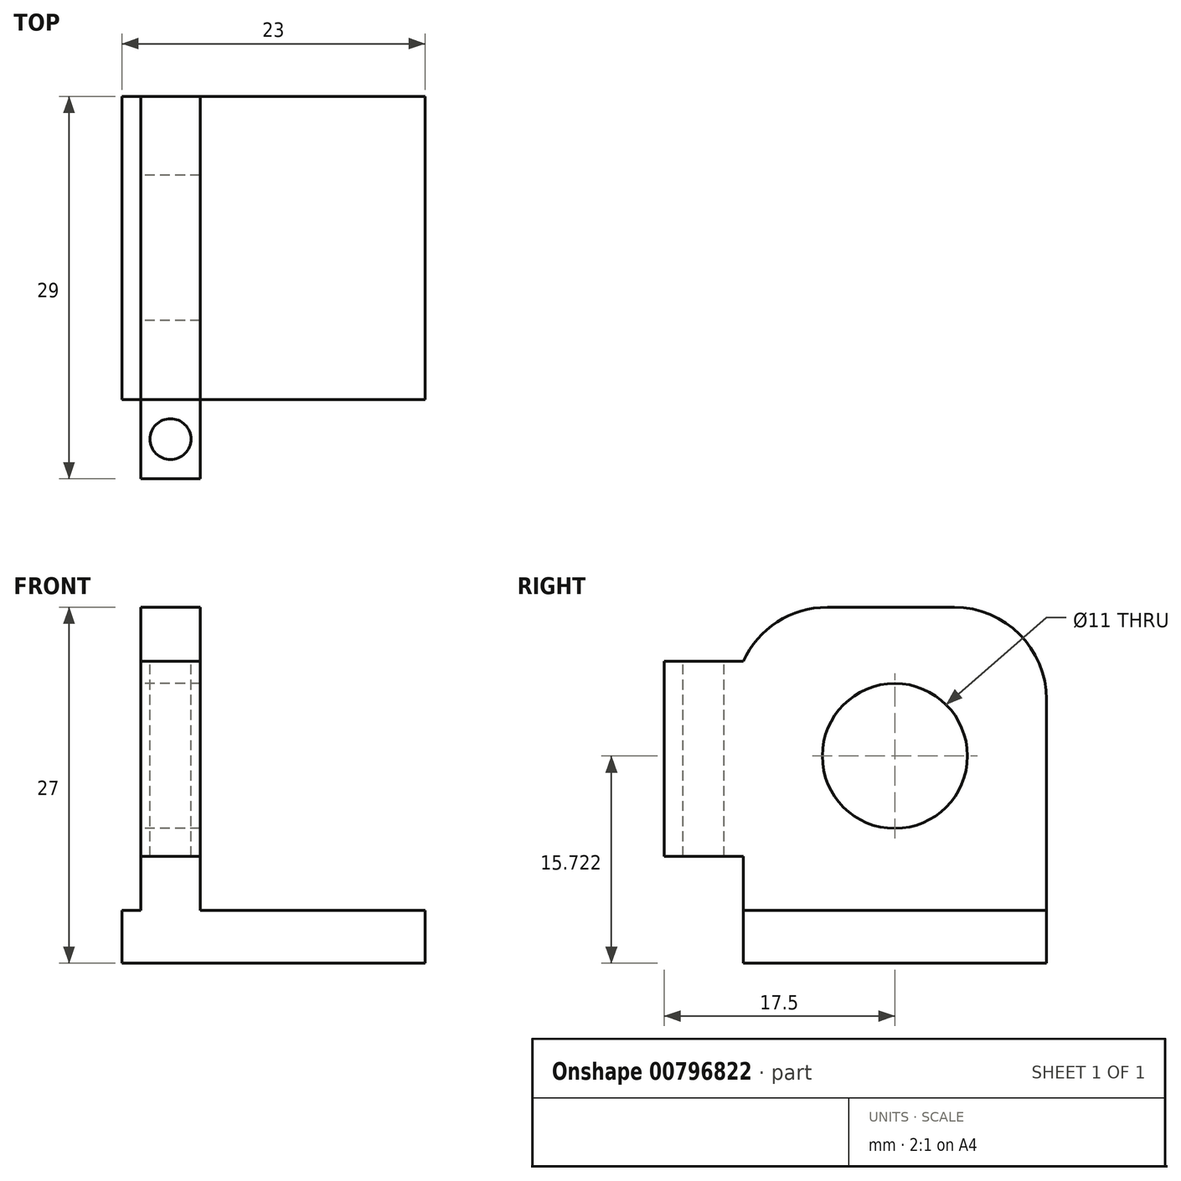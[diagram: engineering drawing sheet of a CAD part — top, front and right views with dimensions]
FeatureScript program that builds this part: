
annotation { "Feature Type Name" : "Feature", "Feature Type Description" : "" }
export const myFeature = defineFeature(function(context is Context, id is Id, definition is map)
    precondition{}
    {
        {
            var Q0;
            Q0=qCreatedBy(makeId("Top.planeOp"),FACE);
            var sketch = newSketch(context, id + "F0", { "sketchPlane" : qUnion([Q0])});
            skLineSegment(sketch, "E0.bottom", {"start": v(-11.5, 11.5) * mm, "end": v(11.5, 11.5) * mm});
            skLineSegment(sketch, "E0.top", {"start": v(-11.5, -11.5) * mm, "end": v(11.5, -11.5) * mm});
            skLineSegment(sketch, "E0.left", {"start": v(-11.5, 11.5) * mm, "end": v(-11.5, -11.5) * mm});
            skLineSegment(sketch, "E0.right", {"start": v(11.5, 11.5) * mm, "end": v(11.5, -11.5) * mm});
            skPoint(sketch, "E0.middle", {"position": v(0, 0) * mm});
            skSolve(sketch);
        }
        {
            var Q0;
            Q0=makeQuery(id+"F0.imprint","IMPRINT",FACE,{"disambiguationData":[TD([[makeQuery(id+"F0.imprint","IMPRINT",EDGE,{"derivedFrom":sQuery(id+"F0.wireOp",EDGE,"E0.bottom")}),-1.0]])]});
            extrude(context, id + "F1", {"entities" : qUnion([Q0]), "depth" : 4 * mm, "offsetDistance" : 25 * mm});
        }
        {
            var Q0;
            Q0=makeQuery(id+"F1.opExtrude","CAP_FACE",FACE,{"disambiguationData":[OSD([sQuery(id+"F0.wireOp",EDGE,"E0.bottom"),sQuery(id+"F0.wireOp",EDGE,"E0.top"),sQuery(id+"F0.wireOp",EDGE,"E0.left"),sQuery(id+"F0.wireOp",EDGE,"E0.right")])],"isStart":false});
            var sketch = newSketch(context, id + "F2", { "sketchPlane" : qUnion([Q0])});
            skLineSegment(sketch, "E1.bottom", {"start": v(-5.56, 11.5) * mm, "end": v(-10.06, 11.5) * mm});
            skLineSegment(sketch, "E1.top", {"start": v(-5.56, -11.5) * mm, "end": v(-10.06, -11.5) * mm});
            skLineSegment(sketch, "E1.left", {"start": v(-5.56, 11.5) * mm, "end": v(-5.56, -11.5) * mm});
            skLineSegment(sketch, "E1.right", {"start": v(-10.06, 11.5) * mm, "end": v(-10.06, -11.5) * mm});
            skSolve(sketch);
        }
        {
            var Q0;
            Q0=makeQuery(id+"F2.imprint","IMPRINT",FACE,{"disambiguationData":[TD([[makeQuery(id+"F2.imprint","IMPRINT",EDGE,{"derivedFrom":sQuery(id+"F2.wireOp",EDGE,"E1.bottom")}),-1.0]])]});
            extrude(context, id + "F3", {"entities" : qUnion([Q0]), "operationType" : NewBodyOperationType.ADD, "depth" : 23 * mm, "offsetDistance" : 25 * mm});
        }
        {
            var Q0;
            Q0=makeQuery(id+"F3.boolean.opBoolean","MERGE",FACE,{"derivedFrom":[makeQuery(id+"F1.opExtrude","SWEPT_FACE",FACE,{"disambiguationData":[OSD([sQuery(id+"F0.wireOp",EDGE,"E0.top")])]}),makeQuery(id+"F3.opExtrude","SWEPT_FACE",FACE,{"disambiguationData":[OSD([sQuery(id+"F2.wireOp",EDGE,"E1.top")])]})]});
            var sketch = newSketch(context, id + "F4", { "sketchPlane" : qUnion([Q0])});
            skLineSegment(sketch, "E2.bottom", {"start": v(-10.06, 22.9) * mm, "end": v(-5.56, 22.9) * mm});
            skLineSegment(sketch, "E2.top", {"start": v(-10.06, 8.1) * mm, "end": v(-5.56, 8.1) * mm});
            skLineSegment(sketch, "E2.left", {"start": v(-10.06, 22.9) * mm, "end": v(-10.06, 8.1) * mm});
            skLineSegment(sketch, "E2.right", {"start": v(-5.56, 22.9) * mm, "end": v(-5.56, 8.1) * mm});
            skPoint(sketch, "E2.middle", {"position": v(-7.8, 15.5) * mm});
            skPoint(sketch, "E2.middle.positionSnap0", {"position": v(-10.06, 15.5) * mm});
            skPoint(sketch, "E2.centerSnap0", {"position": v(-10.06, 15.5) * mm});
            skSolve(sketch);
        }
        {
            var Q0;
            Q0=makeQuery(id+"F4.imprint","IMPRINT",FACE,{"disambiguationData":[TD([[makeQuery(id+"F4.imprint","IMPRINT",EDGE,{"derivedFrom":sQuery(id+"F4.wireOp",EDGE,"E2.bottom")}),-1.0]])]});
            extrude(context, id + "F5", {"entities" : qUnion([Q0]), "operationType" : NewBodyOperationType.ADD, "depth" : 6 * mm, "offsetDistance" : 25 * mm});
        }
        {
            var Q0;
            Q0=makeQuery(id+"F5.boolean.opBoolean","MERGE",FACE,{"derivedFrom":[makeQuery(id+"F3.opExtrude","SWEPT_FACE",FACE,{"disambiguationData":[OSD([sQuery(id+"F2.wireOp",EDGE,"E1.right")])]}),makeQuery(id+"F5.opExtrude","SWEPT_FACE",FACE,{"disambiguationData":[OSD([sQuery(id+"F4.wireOp",EDGE,"E2.left")])]})]});
            var sketch = newSketch(context, id + "F6", { "sketchPlane" : qUnion([Q0])});
            skCircle(sketch, "E3", {"center": v(0, 15.72) * mm, "radius": 5.5 * mm});
            skSolve(sketch);
        }
        {
            var Q0;
            Q0=sQuery(id+"F6.wireOp",VERTEX,"E3.center");
            var Q1;
            Q1=makeQuery(id+"F1.opExtrude","SWEPT_BODY",BODY,{"disambiguationData":[OSD([sQuery(id+"F0.wireOp",EDGE,"E0.bottom"),sQuery(id+"F0.wireOp",EDGE,"E0.top"),sQuery(id+"F0.wireOp",EDGE,"E0.left"),sQuery(id+"F0.wireOp",EDGE,"E0.right")])]});
            hole(context, id + "F7", {"style" : HoleStyle.SIMPLE, "endStyle" : HoleEndStyle.THROUGH, "holeDiameter" : 11 * mm, "majorDiameter" : 5 * mm, "isTappedThrough" : true, "tappedDepth" : 12 * mm, "tapClearance" : 3, "locations" : qUnion([Q0]), "scope" : qUnion([Q1])});
        }
        {
            var Q0;
            Q0=makeQuery(id+"F5.opExtrude","SWEPT_FACE",FACE,{"disambiguationData":[OSD([sQuery(id+"F4.wireOp",EDGE,"E2.bottom")])]});
            var sketch = newSketch(context, id + "F8", { "sketchPlane" : qUnion([Q0])});
            skCircle(sketch, "E4", {"center": v(-7.8, -14.5) * mm, "radius": 1.55 * mm});
            skPoint(sketch, "E4.centerSnap0", {"position": v(-7.8, -17.5) * mm});
            skPoint(sketch, "E4.centerSnap1", {"position": v(-5.56, -14.5) * mm});
            skSolve(sketch);
        }
        {
            var Q0;
            Q0=sQuery(id+"F8.wireOp",VERTEX,"E4.center");
            var Q1;
            Q1=makeQuery(id+"F1.opExtrude","SWEPT_BODY",BODY,{"disambiguationData":[OSD([sQuery(id+"F0.wireOp",EDGE,"E0.bottom"),sQuery(id+"F0.wireOp",EDGE,"E0.top"),sQuery(id+"F0.wireOp",EDGE,"E0.left"),sQuery(id+"F0.wireOp",EDGE,"E0.right")])]});
            hole(context, id + "F9", {"style" : HoleStyle.SIMPLE, "endStyle" : HoleEndStyle.THROUGH, "holeDiameter" : 3.1 * mm, "majorDiameter" : 5 * mm, "isTappedThrough" : true, "tappedDepth" : 12 * mm, "tapClearance" : 3, "locations" : qUnion([Q0]), "scope" : qUnion([Q1])});
        }
        {
            var Q0;
            Q0=makeQuery(id+"F3.opExtrude","CAP_EDGE",EDGE,{"disambiguationData":[OSD([sQuery(id+"F2.wireOp",EDGE,"E1.bottom")])],"isStart":false});
            var Q1;
            Q1=makeQuery(id+"F3.opExtrude","CAP_EDGE",EDGE,{"disambiguationData":[OSD([sQuery(id+"F2.wireOp",EDGE,"E1.top")])],"isStart":false});
            fillet(context, id + "F10", {"entities" : qUnion([Q0, Q1]), "radius" : 7 * mm, "tangentPropagation" : true, "allowEdgeOverflow" : false});
        }
    });
